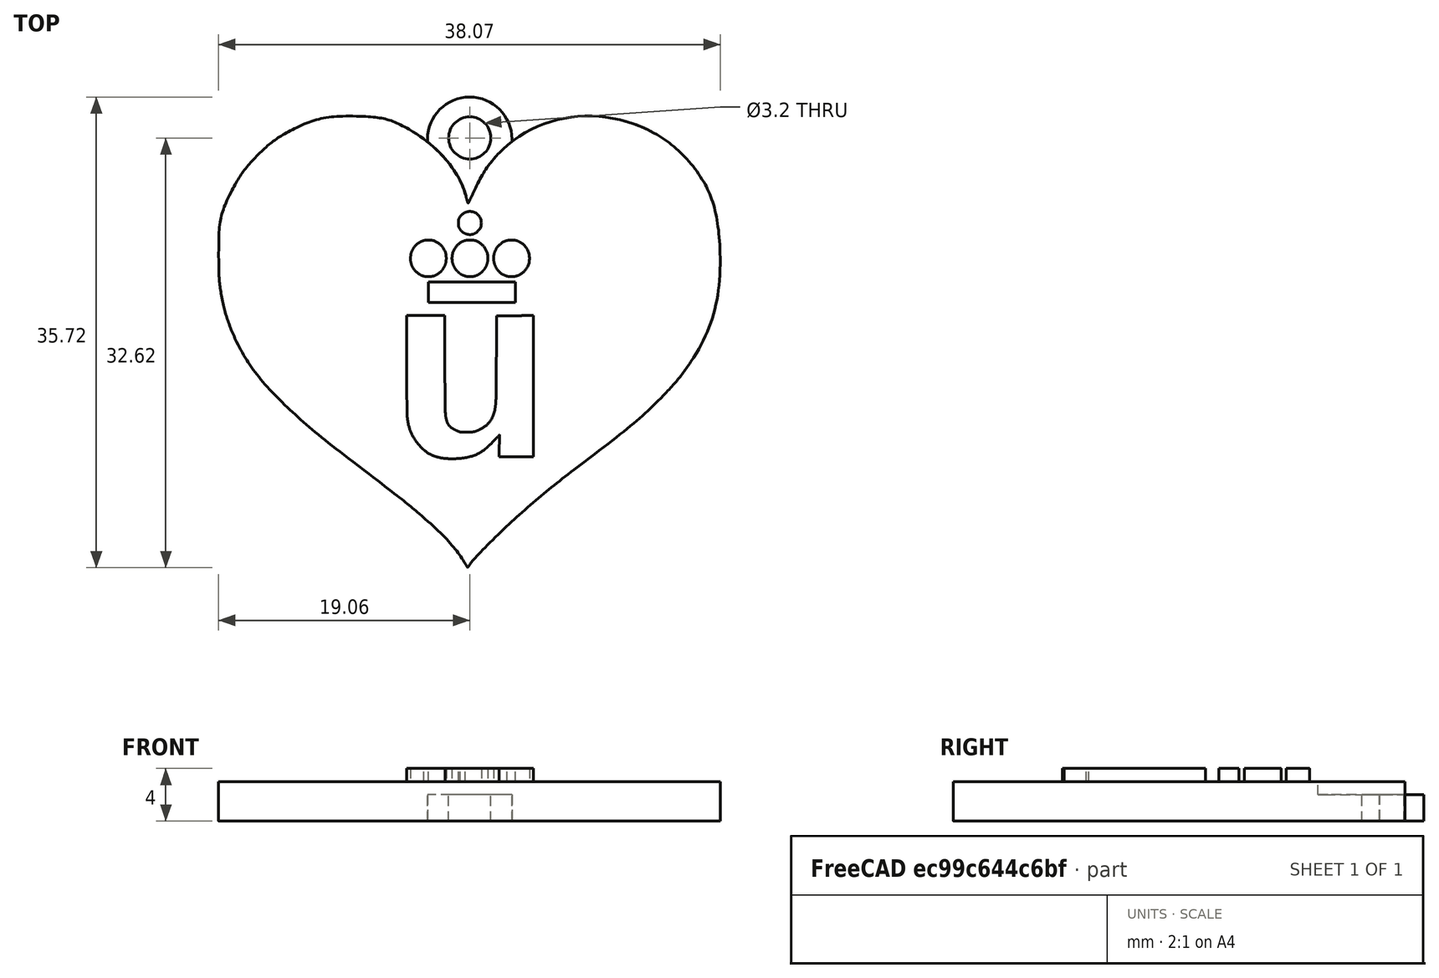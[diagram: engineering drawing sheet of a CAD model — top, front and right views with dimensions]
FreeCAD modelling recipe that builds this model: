
FCSTD DOCUMENT  (FreeCAD 0.17R13217 (Git))
Label: heart-urjc
License: All rights reserved
LicenseURL: http://en.wikipedia.org/wiki/All_rights_reserved
objects: Part::Feature×7, Part::Extrusion×7, Part::MultiFuse×4, Part::Cylinder×2, Part::Box×1, Part::Cut×1, Part::FeaturePython×1
note: 23 computed .brp shape members not serialized (recipe doc carries the construction recipe); baked Part::Feature solids carry a one-line shape summary decoded from their .brp

FEATURE [Part::Feature] path4147
  shape: bbox 38.16 x 34.57 x 2e-07 mm, 0 faces, 0 solids (baked)
FEATURE [Part::Extrusion] Extrude
  Base = -> path4147
  Dir = (0,0,-1)
  DirMode = 2
  FaceMakerClass = Part::FaceMakerBullseye
  LengthFwd = 3
  LengthRev = 0
  Placement = pos=(-19.2,1.8,0) rot=(0,0,1;0rad)
  Reversed = true
  Solid = true
  Symmetric = false
FEATURE [Part::Box] Box  label="Cubo"
  AttacherType = Attacher::AttachEngine3D
  Height = 2
  Length = 6.4
  Placement = pos=(-3.2,-6.6,0) rot=(0,0,1;0rad)
  Width = 6.5
FEATURE [Part::Cylinder] Cylinder  label="Cilindro"
  Angle = 360
  AttacherType = Attacher::AttachEngine3D
  Height = 2
  Placement = pos=(0,-0.1,0) rot=(0,0,1;0rad)
  Radius = 3.2
FEATURE [Part::MultiFuse] Fusion
  Refine = true
  Shapes = -> [Box,Cylinder]
FEATURE [Part::Cylinder] Cylinder001  label="Cilindro001"
  Angle = 360
  AttacherType = Attacher::AttachEngine3D
  Height = 10
  Placement = pos=(0,0,-3.6) rot=(0,0,1;0rad)
  Radius = 1.6
FEATURE [Part::Cut] Cut
  Base = -> Fusion
  Refine = true
  Tool = -> Cylinder001
FEATURE [Part::MultiFuse] Fusion001  label="Corazon-colgante-blanco"
  Refine = true
  Shapes = -> [Extrude,Cut]
FEATURE [Part::Feature] path4159
  shape: bbox 16.02 x 18.13 x 2e-07 mm, 0 faces, 0 solids (baked)
FEATURE [Part::Feature] path4157
  shape: bbox 10.99 x 2.589 x 2e-07 mm, 0 faces, 0 solids (baked)
FEATURE [Part::Feature] path4155
  shape: bbox 4.554 x 4.689 x 2e-07 mm, 0 faces, 0 solids (baked)
FEATURE [Part::Feature] path4153
  shape: bbox 4.636 x 4.66 x 2e-07 mm, 0 faces, 0 solids (baked)
FEATURE [Part::Feature] path4151
  shape: bbox 4.637 x 4.659 x 2e-07 mm, 0 faces, 0 solids (baked)
FEATURE [Part::Feature] path4147001
  shape: bbox 3.07 x 3.007 x 2e-07 mm, 0 faces, 0 solids (baked)
FEATURE [Part::Extrusion] Extrude001
  Base = -> path4159
  Dir = (0,0,-1)
  DirMode = 2
  FaceMakerClass = Part::FaceMakerBullseye
  LengthFwd = 1
  LengthRev = 0
  Reversed = true
  Solid = true
  Symmetric = false
FEATURE [Part::Extrusion] Extrude002
  Base = -> path4157
  Dir = (0,0,-1)
  DirMode = 2
  FaceMakerClass = Part::FaceMakerBullseye
  LengthFwd = 1
  LengthRev = 0
  Reversed = true
  Solid = true
  Symmetric = false
FEATURE [Part::Extrusion] Extrude003
  Base = -> path4155
  Dir = (0,0,-1)
  DirMode = 2
  FaceMakerClass = Part::FaceMakerBullseye
  LengthFwd = 1
  LengthRev = 0
  Reversed = true
  Solid = true
  Symmetric = false
FEATURE [Part::Extrusion] Extrude004
  Base = -> path4153
  Dir = (0,0,-1)
  DirMode = 2
  FaceMakerClass = Part::FaceMakerBullseye
  LengthFwd = 1
  LengthRev = 0
  Reversed = true
  Solid = true
  Symmetric = false
FEATURE [Part::Extrusion] Extrude005
  Base = -> path4151
  Dir = (0,0,-1)
  DirMode = 2
  FaceMakerClass = Part::FaceMakerBullseye
  LengthFwd = 1
  LengthRev = 0
  Reversed = true
  Solid = true
  Symmetric = false
FEATURE [Part::Extrusion] Extrude006
  Base = -> path4147001
  Dir = (0,0,-1)
  DirMode = 2
  FaceMakerClass = Part::FaceMakerBullseye
  LengthFwd = 1
  LengthRev = 0
  Reversed = true
  Solid = true
  Symmetric = false
FEATURE [Part::MultiFuse] Fusion002
  Refine = true
  Shapes = -> [Extrude001,Extrude003,Extrude004,Extrude005,Extrude006,Extrude002]
FEATURE [Part::FeaturePython] Clone  label="Fusion003"  # Draft clone (typed FeaturePython)
  AttacherType = Attacher::AttachEngine3D
  Fuse = false
  Objects = -> [Fusion002]
  Placement = pos=(-4.94645,-5.41308,3) rot=(0,0,1;0rad)
  Scale = (0.6,0.6,1)
FEATURE [Part::MultiFuse] Fusion003  label="Fusion004"
  Refine = true
  Shapes = -> [Fusion001,Clone]
